# Revit family: Gira_228228
name_source: partatom
category: Electrical Fixtures
revit_build: Autodesk Revit 2017 (Build: 20160225_1515(x64)
units: mm (PartAtom-declared; Revit-internal decimal feet)

## family parameters
Cut with Voids When Loaded = No
Host = Face
Maintain Annotation Orientation = Yes
Part Type = Normal
Room Calculation Point = No
Round Connector Dimension = Use Diameter
Shared = No

## types (1)
- Speaker RDS FM radio System 55 anthra.
    Assembly arrangement = Basic element with housing top
    Available = No
    BIM (1) = https://media.stage.bim.site und Tasten.rfa?public/gira/36a6b08/Sys55_Komplettgerät_Schalten und Tasten.rfa
    Category = Electronic insert for domestic switching devices
    Colour = Anthracite
    Data sheet (1) = https://katalog.gira.de
    Default Elevation = 1219 mm
    Description = Spk.FM radio RDS Sys55 AN,Speaker for the RDS flush-mounted radio,,anthracite,Features:,- Speaker for connection to the Gira RDS flush-mounted radio.
    GTIN = 4010337076261
    HAN = 228228
    Halogen free = No
    HeinzeBIM = https://bimportal.heinze.de
    Manufacturer = Gira
    Manufacturer URL = https://www.gira.de
    Material = Other
    Material quality = Other
    Model = Radio
    Mounting method = Flush mounted (plaster)
    Name = Speaker RDS FM radio System 55 anthra.
    Surface finishing = Glossy
    Surface protection = Other
    Type of fastening = Mounting with claw and screw
    URL = http://katalog.gira.de

## geometry (parser evidence)
native form markers: Blend x2, Sweep x8
no freeform markers — native parametric forms only
